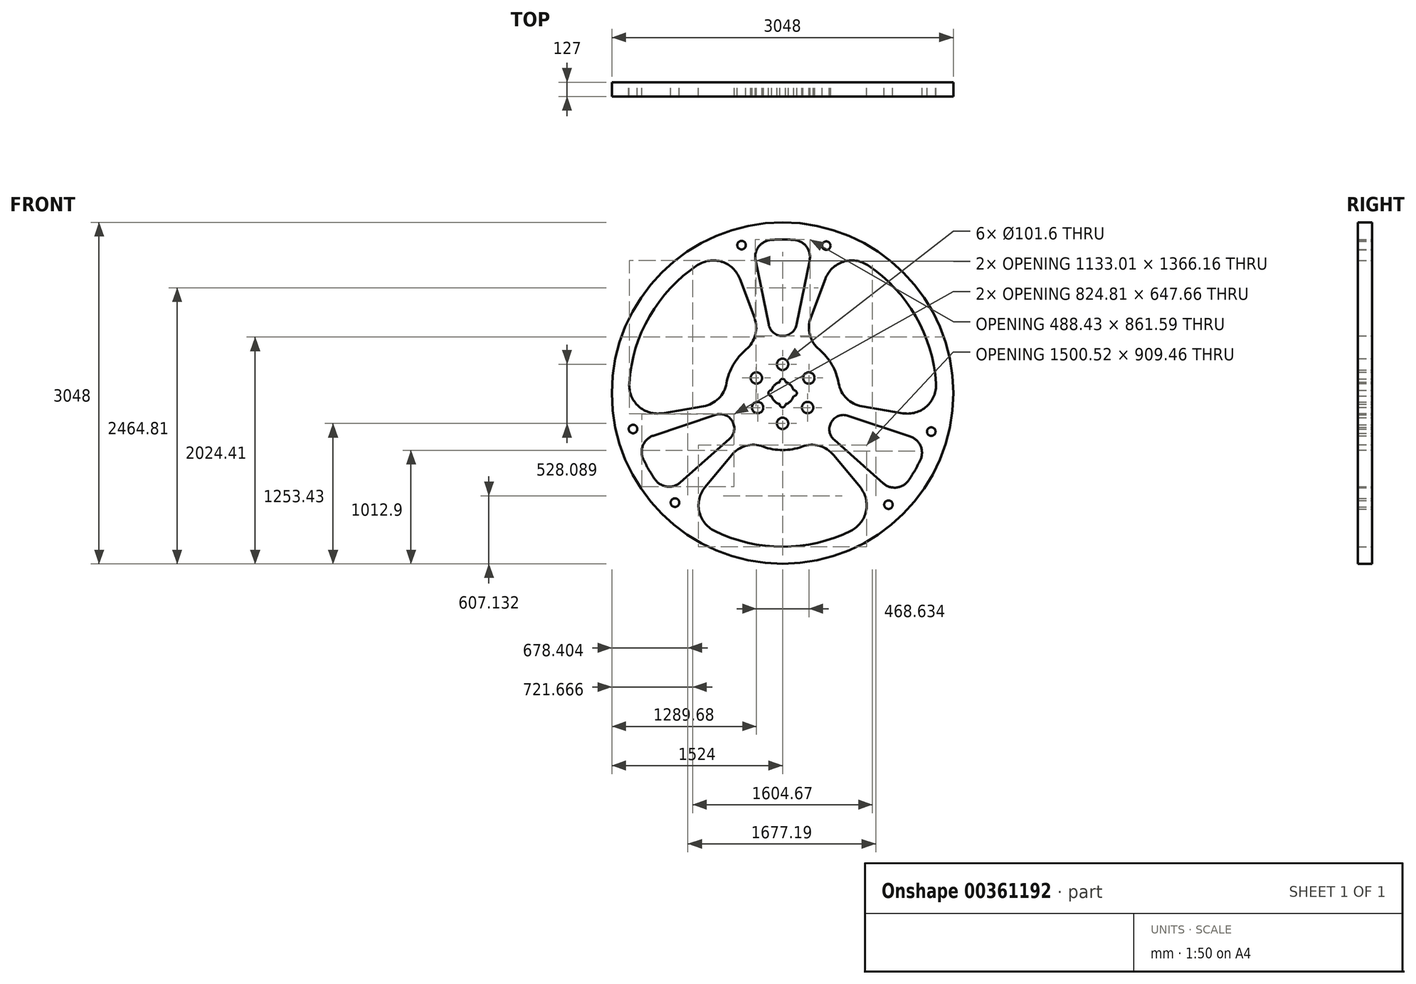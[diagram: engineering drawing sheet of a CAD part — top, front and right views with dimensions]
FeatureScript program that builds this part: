
annotation { "Feature Type Name" : "Feature", "Feature Type Description" : "" }
export const myFeature = defineFeature(function(context is Context, id is Id, definition is map)
    precondition{}
    {
        {
            var Q0;
            Q0=qCreatedBy(makeId("Front.planeOp"),FACE);
            var sketch = newSketch(context, id + "F0", { "sketchPlane" : qUnion([Q0])});
            skCircle(sketch, "E0", {"center": v(0, 0) * mm, "radius": 1524 * mm});
            skArc(sketch, "E1", {"start": v(-759.76, 1141.95) * mm, "mid": v(-1187.84, 685.8) * mm, "end": v(-1368.84, 87) * mm});
            skLineSegment(sketch, "E2", {"start": v(-124.45, 611.7) * mm, "end": v(-241.16, 1185.35) * mm});
            skLineSegment(sketch, "E3", {"start": v(124.45, 611.7) * mm, "end": v(241.16, 1185.35) * mm});
            skArc(sketch, "E4", {"start": v(-103.3, 1367.7) * mm, "mid": v(-213.39, 1307.65) * mm, "end": v(-241.16, 1185.35) * mm});
            skArc(sketch, "E5", {"start": v(241.16, 1185.35) * mm, "mid": v(213.39, 1307.65) * mm, "end": v(103.3, 1367.7) * mm});
            skArc(sketch, "E6.trimOffspring", {"start": v(103.3, 1367.7) * mm, "mid": v(0, 1371.6) * mm, "end": v(-103.3, 1367.7) * mm});
            skArc(sketch, "E7", {"start": v(-124.45, 611.7) * mm, "mid": v(0, 510.01) * mm, "end": v(124.45, 611.7) * mm});
            skLineSegment(sketch, "E8", {"start": v(-323.13, 391.99) * mm, "end": v(-323.16, 392.03) * mm});
            skArc(sketch, "E9.1.0", {"start": v(-1139.69, -769.05) * mm, "mid": v(-1032.63, -834.36) * mm, "end": v(-912.84, -797.27) * mm});
            skArc(sketch, "E9.1.1", {"start": v(-1242.99, -590.13) * mm, "mid": v(-1194.71, -681.54) * mm, "end": v(-1139.69, -769.05) * mm});
            skArc(sketch, "E9.1.2", {"start": v(-1154, -379.56) * mm, "mid": v(-1246.02, -464.76) * mm, "end": v(-1242.99, -590.13) * mm});
            skLineSegment(sketch, "E9.1.3", {"start": v(-598.84, -193.8) * mm, "end": v(-1154, -379.56) * mm});
            skArc(sketch, "E9.1.4", {"start": v(-474.39, -409.36) * mm, "mid": v(-448.56, -250.75) * mm, "end": v(-598.84, -193.8) * mm});
            skLineSegment(sketch, "E9.1.5", {"start": v(-474.39, -409.36) * mm, "end": v(-912.84, -797.27) * mm});
            skArc(sketch, "E9.2.0", {"start": v(1229, -598.21) * mm, "mid": v(1232.02, -472.84) * mm, "end": v(1140, -387.65) * mm});
            skArc(sketch, "E9.2.1", {"start": v(1125.7, -777.13) * mm, "mid": v(1180.72, -689.62) * mm, "end": v(1229, -598.21) * mm});
            skArc(sketch, "E9.2.2", {"start": v(898.84, -805.35) * mm, "mid": v(1018.63, -842.45) * mm, "end": v(1125.7, -777.13) * mm});
            skLineSegment(sketch, "E9.2.3", {"start": v(460.4, -417.45) * mm, "end": v(898.84, -805.35) * mm});
            skArc(sketch, "E9.2.4", {"start": v(584.84, -201.9) * mm, "mid": v(434.56, -258.83) * mm, "end": v(460.4, -417.45) * mm});
            skLineSegment(sketch, "E9.2.5", {"start": v(584.84, -201.9) * mm, "end": v(1140, -387.65) * mm});
            skPoint(sketch, "E9.center", {"position": v(-4.67, 0.15) * mm});
            skLineSegment(sketch, "E10", {"start": v(-456.97, -554.35) * mm, "end": v(-692.28, -839.8) * mm});
            skLineSegment(sketch, "E11", {"start": v(456.97, -554.35) * mm, "end": v(692.28, -839.8) * mm});
            skArc(sketch, "E12", {"start": v(-173.99, -477.28) * mm, "mid": v(0, -508) * mm, "end": v(173.99, -477.28) * mm});
            skArc(sketch, "E13", {"start": v(-173.99, -477.28) * mm, "mid": v(-327.73, -470.84) * mm, "end": v(-456.97, -554.35) * mm});
            skArc(sketch, "E14", {"start": v(609.08, -1228.95) * mm, "mid": v(744.67, -1054.47) * mm, "end": v(692.28, -839.8) * mm});
            skArc(sketch, "E15.trimOffspring", {"start": v(-692.28, -839.8) * mm, "mid": v(-744.67, -1054.47) * mm, "end": v(-609.08, -1228.95) * mm});
            skArc(sketch, "E16.trimOffspring", {"start": v(456.97, -554.35) * mm, "mid": v(327.73, -470.84) * mm, "end": v(173.99, -477.28) * mm});
            skArc(sketch, "E17.trimOffspring", {"start": v(500.33, 87.96) * mm, "mid": v(439.94, 254) * mm, "end": v(326.34, 389.31) * mm});
            skArc(sketch, "E18.trimOffspring", {"start": v(-609.08, -1228.95) * mm, "mid": v(0, -1371.6) * mm, "end": v(609.08, -1228.95) * mm});
            skArc(sketch, "E19.1.0", {"start": v(1368.84, 87) * mm, "mid": v(1187.84, 685.8) * mm, "end": v(759.76, 1141.95) * mm});
            skArc(sketch, "E19.1.1", {"start": v(759.76, 1141.95) * mm, "mid": v(540.86, 1172.14) * mm, "end": v(381.15, 1019.43) * mm});
            skLineSegment(sketch, "E19.1.2", {"start": v(251.6, 672.92) * mm, "end": v(381.15, 1019.43) * mm});
            skArc(sketch, "E19.1.3", {"start": v(251.6, 672.92) * mm, "mid": v(243.9, 519.24) * mm, "end": v(326.34, 389.31) * mm});
            skArc(sketch, "E19.1.5", {"start": v(500.33, 87.96) * mm, "mid": v(571.62, -48.4) * mm, "end": v(708.57, -118.57) * mm});
            skLineSegment(sketch, "E19.1.6", {"start": v(708.57, -118.57) * mm, "end": v(1073.43, -179.63) * mm});
            skArc(sketch, "E19.1.7", {"start": v(1073.43, -179.63) * mm, "mid": v(1285.53, -117.67) * mm, "end": v(1368.84, 87) * mm});
            skArc(sketch, "E19.2.1", {"start": v(-1368.84, 87) * mm, "mid": v(-1285.53, -117.67) * mm, "end": v(-1073.43, -179.63) * mm});
            skLineSegment(sketch, "E19.2.2", {"start": v(-708.57, -118.57) * mm, "end": v(-1073.43, -179.63) * mm});
            skArc(sketch, "E19.2.3", {"start": v(-708.57, -118.57) * mm, "mid": v(-571.62, -48.4) * mm, "end": v(-500.33, 87.96) * mm});
            skArc(sketch, "E19.2.4", {"start": v(-326.34, 389.31) * mm, "mid": v(-439.94, 254) * mm, "end": v(-500.33, 87.96) * mm});
            skArc(sketch, "E19.2.5", {"start": v(-326.34, 389.31) * mm, "mid": v(-243.9, 519.24) * mm, "end": v(-251.6, 672.92) * mm});
            skLineSegment(sketch, "E19.2.6", {"start": v(-251.6, 672.92) * mm, "end": v(-381.15, 1019.43) * mm});
            skArc(sketch, "E19.2.7", {"start": v(-381.15, 1019.43) * mm, "mid": v(-540.86, 1172.14) * mm, "end": v(-759.76, 1141.95) * mm});
            skCircle(sketch, "E20", {"center": v(0, 0) * mm, "radius": 381 * mm});
            skCircle(sketch, "E21", {"center": v(0, -270.57) * mm, "radius": 50.8 * mm});
            skCircle(sketch, "E22.1.0", {"center": v(234.32, 135.28) * mm, "radius": 50.8 * mm});
            skCircle(sketch, "E22.2.0", {"center": v(-234.32, 135.28) * mm, "radius": 50.8 * mm});
            skCircle(sketch, "E23", {"center": v(0, 257.52) * mm, "radius": 50.8 * mm});
            skCircle(sketch, "E24.1.0", {"center": v(-223.02, -128.76) * mm, "radius": 50.8 * mm});
            skCircle(sketch, "E24.2.0", {"center": v(223.02, -128.76) * mm, "radius": 50.8 * mm});
            skArc(sketch, "E25", {"start": v(-98.43, -25.2) * mm, "mid": v(-71.84, -71.84) * mm, "end": v(-25.2, -98.42) * mm});
            skArc(sketch, "E26", {"start": v(25.2, 98.42) * mm, "mid": v(0, 127) * mm, "end": v(-25.2, 98.43) * mm});
            skArc(sketch, "E27", {"start": v(-98.43, 25.2) * mm, "mid": v(-127, 0) * mm, "end": v(-98.43, -25.2) * mm});
            skArc(sketch, "E28", {"start": v(-25.2, -98.42) * mm, "mid": v(0, -127) * mm, "end": v(25.2, -98.43) * mm});
            skArc(sketch, "E29", {"start": v(98.42, -25.2) * mm, "mid": v(127, 0) * mm, "end": v(98.43, 25.2) * mm});
            skArc(sketch, "E30.trimOffspring", {"start": v(-25.2, 98.43) * mm, "mid": v(-71.84, 71.84) * mm, "end": v(-98.43, 25.2) * mm});
            skArc(sketch, "E31.trimOffspring", {"start": v(25.2, -98.43) * mm, "mid": v(71.84, -71.84) * mm, "end": v(98.42, -25.2) * mm});
            skArc(sketch, "E32.trimOffspring", {"start": v(98.43, 25.2) * mm, "mid": v(71.84, 71.84) * mm, "end": v(25.2, 98.42) * mm});
            skCircle(sketch, "E33", {"center": v(389.9, 1316.4) * mm, "radius": 38.1 * mm});
            skCircle(sketch, "E34", {"center": v(-366.35, 1320.93) * mm, "radius": 38.1 * mm});
            skCircle(sketch, "E35.1.0", {"center": v(-960.78, -977.74) * mm, "radius": 38.1 * mm});
            skCircle(sketch, "E35.1.1", {"center": v(-1335, -320.53) * mm, "radius": 38.1 * mm});
            skCircle(sketch, "E35.2.0", {"center": v(1327.14, -343.2) * mm, "radius": 38.1 * mm});
            skCircle(sketch, "E35.2.1", {"center": v(945.09, -995.87) * mm, "radius": 38.1 * mm});
            skPoint(sketch, "E36.orphan", {"position": v(-1762.2, -423.1) * mm});
            skPoint(sketch, "E37.orphan", {"position": v(-564.35, 2034.82) * mm});
            skSolve(sketch);
        }
        {
            var Q0;
            Q0=makeQuery(id+"F0.imprint","IMPRINT",FACE,{"disambiguationData":[TD([[makeQuery(id+"F0.imprint","IMPRINT",EDGE,{"derivedFrom":sQuery(id+"F0.wireOp",EDGE,"E0")}),1.0]])]});
            var Q1;
            Q1=makeQuery(id+"F0.imprint","IMPRINT",FACE,{"disambiguationData":[TD([[makeQuery(id+"F0.imprint","IMPRINT",EDGE,{"derivedFrom":sQuery(id+"F0.wireOp",EDGE,"E20")}),1.0]])]});
            extrude(context, id + "F1", {"entities" : qUnion([Q0, Q1]), "depth" : 127 * mm});
        }
    });
